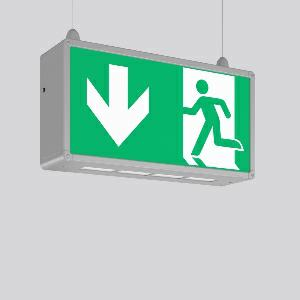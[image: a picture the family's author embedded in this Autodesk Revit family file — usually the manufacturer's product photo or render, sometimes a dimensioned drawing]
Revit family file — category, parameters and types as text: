
# Revit family: rechteck_seilpendel_671351_004_2422
name_source: partatom
category: Lighting Fixtures
units: mm (PartAtom-declared; Revit-internal decimal feet)

## family parameters
Cut with Voids When Loaded = No
Host = Face
Light Source = No
Part Type = Normal
Room Calculation Point = No
Round Connector Dimension = Use Diameter
Shared = No

## types (1)
- RECHTECK seilpendel
    Apparent Load = 0 VA
    Default Elevation = 1800 mm
    Description = Series: RECHTECK
Rectangular pendant luminaire in classic design. For escape route identification. Housing: aluminium, with plastic corner connectors. Display panels: plastic, opal, with motifs on one side/on both sides. Pendant luminaires (suspension provided on site) ready for connection to two suspension cables or chains. Electronic ballast included. Self-contained system with automatic self-test. Please indicate legend number when placing your order! 
Colour: anodised aluminium
Length: 485 mm
Width: 125 mm
Height: 250 mm
Weight: 3.11 kg
Operating mode: maintained power mode
Viewing Distance: 43 m
Duration time: 3 h
Lamp: LED
Socket: without socket
Colour temperature: 6500K
Colour rendering index (CRI): 70
System power: 9.1 W
Control gear: Regulated power supply
Protection class: I
Type of protection: IP 44
    Height = 250 mm
    Lamp = 0 x
    Length = 485 mm
    Luminous efficacy = 0 lm/W
    Manufacturer = RZB
    ModVariant = No
    Model = 671351.004
    Mounting Place = Ceiling
    Mounting Type = Pendant
    Number of Poles = 1
    OnlyDefault = Yes
    Power Factor = 1
    Product Name = RECHTECK seilpendel
    Product group = Pendant luminaires
    ProductGroupID = 902
    Protection Class = Protection class I
    Protection Degree = IP 44
    RLX_Detail_Level = 1
    RLX_Emergency_Light_Flux = 0 lm
    RLX_Emergency_Type = 0
    RLX_Emergency_Type_DB = No
    RlxData = <blob elided: 56809 chars, md5=c4c4c8e4>
    Standby Power = 0 W
    System Light Flux = 0 lm
    System Power = 0 W
    Type Comments = Product without accessories
    Type Image = 671351.004.jpg
    URL = http://relux.com
    VarID = ---
    Voltage = 230 V
    Voltage Range = 220-240 V
    Weight = 0.00 kg
    Width = 125 mm

## geometry (parser evidence)
native form markers: Blend x4, Sweep x13
no freeform markers — native parametric forms only
